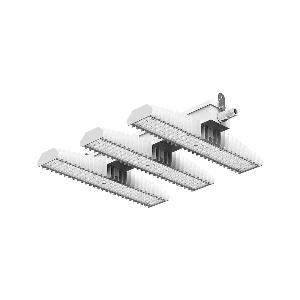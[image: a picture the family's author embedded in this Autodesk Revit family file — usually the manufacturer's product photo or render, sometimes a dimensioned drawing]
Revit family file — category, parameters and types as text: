
# Revit family: 3f_filippi_-_3f_lem_ho_ampio_3f_filippi_-_58955_-_3f_lem_3_ho_led_210_cr_ampio
name_source: partatom
category: Lighting Fixtures
units: mm (PartAtom-declared; Revit-internal decimal feet)

## family parameters
Cut with Voids When Loaded = No
Host = Face
Light Source = No
Part Type = Normal
Room Calculation Point = No
Round Connector Dimension = Use Diameter
Shared = No

## types (1)
- 3F Filippi - 3F LEM HO Ampio (1 x LED, 33909 lm, 207 W, 4000 K)
    Apparent Load = 207 VA
    Approval mark = CE
    CIE Flux Codes = 60 92 99 100 100
    Color Rendering = 80
    Color Temperature = 4000 K
    Control Gear = Electronic ballast
    Default Elevation = 1800 mm
    Description = Industrial luminaire with high light output and high luminous efficiency designed with the most innovative technologies for environments with temperature up to 55°C.

ILLUMINOTECHNICAL
Luminous efficiency 100% (DLOR 100%, ULOR 0%).
Initial luminous flux of the luminaire 33909 lm.
Direct symmetric wide distribution: the illuminated area has a rectangular shape.
Installation Interdistance Transv.D = 1.58 x hu - Long.D = 1.45 x hu.
Tabular UGR (CIE 117 - 4H-8H; S=0.25H; 70/50/20): RUG 24.2 - 25.2.
Beam angle: 93° - 99°.
Luminous efficacy 164 lm/W.
Lifetime (L93/B10): 30000 h. (tq+25°C)
Lifetime (L90/B10): 50000 h. (tq+25°C)
Lifetime (L85/B10): 80000 h. (tq+25°C)
Lifetime (L80/B10): 100000 h. (tq+25°C)
Lifetime (L85/B10): 50000 h. (tq+55°C)
Sudden decreased luminous flux after 50000 hours: 0% (C0).
Photobiological safety in compliance with IEC/TR 62778: RG0 risk exempt, (IEC 62471).
In compliance with IEC/EN 62722-2-1 - IEC/EN 62717 standards.

SOURCE
3 Mid-Power linear LED modules 70W/840.
Energy efficiency class (UE 2019/2020 - UE 2019/2015): C.
CIE 13.3 Colour rendering index: CRI >80 (R9 <50%).
IES TM-30 Fidelity Index: Rf = 84 Rg = 95.
CCT nominal colour temperature 4000 K.
Colour initial tolerance (MacAdam): SDCM 3.

MECHANICAL
Passive modular heatsinks in die-casted aluminium, painted in white colour.
To optimize the thermal management of the LED module, the heatsinks are oversized and provided with self-cleaning of cooling fins.
Wiring body in aluminium and galvanised steel anchored solidly to the sinks and thermally separated.
3F Lens lenses with high luminous efficiency, transparent methacrylate (PMMA), fixed to the LED modules.
Fixing brackets in stainless steel.
Luminaire with limited surface temperature. - D - (EN 60598-2-24)
Dimensions: 657x542 mm, height 129 mm. Weight 13.67 kg.
IP65 protection degree.
Mechanical strength to impacts IK06 (1 joule).
Glow-wire test resistance 650°C.

ELECTRICAL
Halogen Free electronic wiring 230V-50/60Hz, power factor 0.97, THD <25%, constant output current, class I, 2 driver.
Power of the luminaire 207 W.
ENEC - CE.
SAFE FLICKER: PstLM=<1 and SVM=<0.4 (IEC TR 61547-1 and IEC TR 63158), to ensure a more comfortable and safe light.
Luminaire compliant with EN 60598-2-22 for power supply from a centralised emergency system CPSS (Central Power Supply System), not incorporated in the luminaire - high risk areas excluded. The default power and flux are 100% in AC and 100% in DC.
Ambient temperature from -30°C to +55°C.
Temperature class T6 max 85°C.
Quick connection via M20 3P connector with 9-13 mm tightening range.
Power unit positioned on a separate compartment by the LED module to ensure optimum temperatures of cabling components, to be inspectable and maintainable.
Relative humidity UR: <85%.

INSTALLATION
Ceiling / Suspended / Wall.
All accessories dedicated to this product are available on the Catalog and on our website www.3F-Filippi.com.

APPLICATIONS
In commercial environments, exhibition and industrial areas, stores, open areas.
Environments in which it is necessary a total protection against falling fragments (eg environments with foodstuffs or machines with moving parts or with extreme temperature changes), use luminaires with polycarbonate lenses.

WARNING
Fixture not suitable for cold stores with an ambient temperature <0°C and/or relative humidity >85%.
Luminaire designed for disposal/recycling at end-of-life.
Replaceable (LED only) light source by a professional. Replaceable control gear by a professional.
    Height = 129 mm
    Lamp = 1 x LED
    Lamp Light Flux = 33909 lm
    Lamp Power = 207 W
    Lamp count = 1
    Length = 657 mm
    Lifetime = 50000 h
    Luminous efficacy = 164 lm/W
    Manufacturer = 3F Filippi
    ModVariant = No
    Model = 3F Filippi - 58955 - 3F LEM 3 HO LED 210 CR AMPIO
    Mounting Place = Ceiling
    Mounting Type = Pendant
    Number of Poles = 1
    OnlyDefault = Yes
    Power Factor = 1
    Product Name = 3F Filippi - 3F LEM HO Ampio
    Product group = pendant luminaire
    ProductGroupID = 9
    Protection Class = Protection class I
    Protection Degree = IP 65
    RLX_Detail_Level = 1
    RLX_Emergency_Light_Flux = 0 lm
    RLX_Emergency_Type = 0
    RLX_Emergency_Type_DB = No
    RlxData = <blob elided: 100605 chars, md5=303becea>
    Socket = socket
    Standby Power = 0 W
    System Light Flux = 33909 lm
    System Power = 207 W
    Type Comments = Product without accessories
    Type Image = 3f_filippi_-_lem_3.jpg
    URL = http://relux.com
    VarID = ---
    Voltage = 0 V
    Weight = 0.00 kg
    Width = 542 mm

## geometry (parser evidence)
native form markers: Blend x4, Sweep x11
no freeform markers — native parametric forms only
